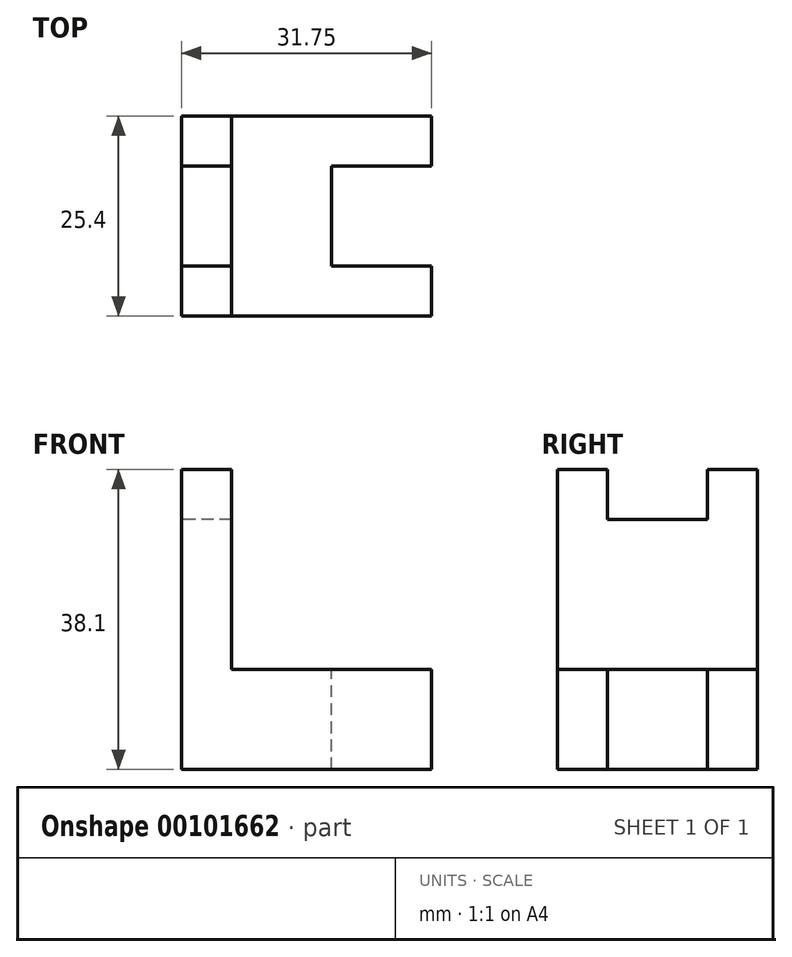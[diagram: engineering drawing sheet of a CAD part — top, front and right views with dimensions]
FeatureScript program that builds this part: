
annotation { "Feature Type Name" : "Feature", "Feature Type Description" : "" }
export const myFeature = defineFeature(function(context is Context, id is Id, definition is map)
    precondition{}
    {
        {
            var Q0;
            Q0=qCreatedBy(makeId("Top.planeOp"),FACE);
            var sketch = newSketch(context, id + "F0", { "sketchPlane" : qUnion([Q0])});
            skLineSegment(sketch, "E0", {"start": v(0, 0) * mm, "end": v(0, 25.4) * mm});
            skLineSegment(sketch, "E1", {"start": v(0, 25.4) * mm, "end": v(31.75, 25.4) * mm});
            skLineSegment(sketch, "E2", {"start": v(31.75, 25.4) * mm, "end": v(31.75, 19.05) * mm});
            skLineSegment(sketch, "E3", {"start": v(31.75, 19.05) * mm, "end": v(19.05, 19.05) * mm});
            skLineSegment(sketch, "E4", {"start": v(19.05, 19.05) * mm, "end": v(19.05, 6.35) * mm});
            skLineSegment(sketch, "E5", {"start": v(19.05, 6.35) * mm, "end": v(31.75, 6.35) * mm});
            skLineSegment(sketch, "E6", {"start": v(31.75, 6.35) * mm, "end": v(31.75, 0) * mm});
            skLineSegment(sketch, "E7", {"start": v(31.75, 0) * mm, "end": v(0, 0) * mm});
            skSolve(sketch);
        }
        {
            var Q0;
            Q0=makeQuery(id+"F0.imprint","IMPRINT",FACE,{"disambiguationData":[TD([[makeQuery(id+"F0.imprint","IMPRINT",EDGE,{"derivedFrom":sQuery(id+"F0.wireOp",EDGE,"E0")}),-1.0]])]});
            extrude(context, id + "F1", {"entities" : qUnion([Q0]), "oppositeDirection" : true, "depth" : 12.7 * mm});
        }
        {
            var Q0;
            Q0=qCreatedBy(makeId("Right.planeOp"),FACE);
            var sketch = newSketch(context, id + "F2", { "sketchPlane" : qUnion([Q0])});
            skLineSegment(sketch, "E8", {"start": v(0, 0) * mm, "end": v(0, 25.4) * mm});
            skLineSegment(sketch, "E9", {"start": v(0, 25.4) * mm, "end": v(6.35, 25.4) * mm});
            skLineSegment(sketch, "E10", {"start": v(6.35, 25.4) * mm, "end": v(6.35, 19.05) * mm});
            skLineSegment(sketch, "E11", {"start": v(6.35, 19.05) * mm, "end": v(19.05, 19.05) * mm});
            skLineSegment(sketch, "E12", {"start": v(19.05, 19.05) * mm, "end": v(19.05, 25.4) * mm});
            skLineSegment(sketch, "E13", {"start": v(19.05, 25.4) * mm, "end": v(25.4, 25.4) * mm});
            skLineSegment(sketch, "E14", {"start": v(25.4, 25.4) * mm, "end": v(25.4, 0) * mm});
            skLineSegment(sketch, "E15", {"start": v(25.4, 0) * mm, "end": v(0, 0) * mm});
            skSolve(sketch);
        }
        {
            var Q0;
            Q0=makeQuery(id+"F2.imprint","IMPRINT",FACE,{"disambiguationData":[TD([[makeQuery(id+"F2.imprint","IMPRINT",EDGE,{"derivedFrom":sQuery(id+"F2.wireOp",EDGE,"E8")}),-1.0]])]});
            extrude(context, id + "F3", {"entities" : qUnion([Q0]), "operationType" : NewBodyOperationType.ADD, "depth" : 6.35 * mm});
        }
    });
